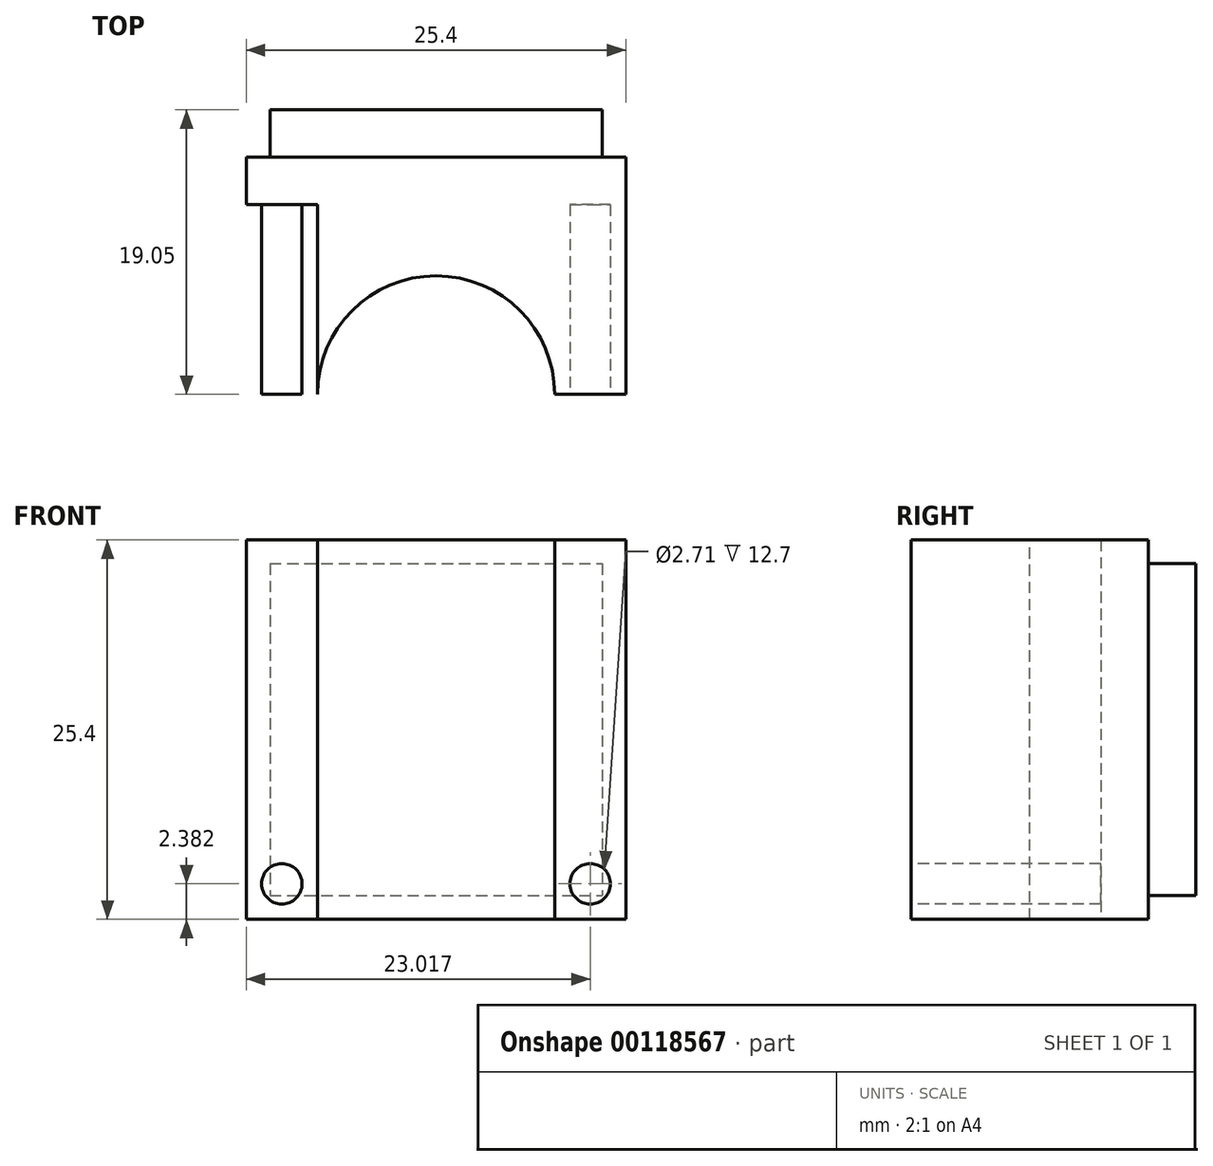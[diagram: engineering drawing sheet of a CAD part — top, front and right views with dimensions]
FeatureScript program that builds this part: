
annotation { "Feature Type Name" : "Feature", "Feature Type Description" : "" }
export const myFeature = defineFeature(function(context is Context, id is Id, definition is map)
    precondition{}
    {
        {
            var Q0;
            Q0=qCreatedBy(makeId("Front.planeOp"),FACE);
            var sketch = newSketch(context, id + "F0", { "sketchPlane" : qUnion([Q0])});
            skLineSegment(sketch, "E0.bottom", {"start": v(12.7, 12.7) * mm, "end": v(-12.7, 12.7) * mm});
            skLineSegment(sketch, "E0.top", {"start": v(12.7, -12.7) * mm, "end": v(-12.7, -12.7) * mm});
            skLineSegment(sketch, "E0.left", {"start": v(12.7, 12.7) * mm, "end": v(12.7, -12.7) * mm});
            skLineSegment(sketch, "E0.right", {"start": v(-12.7, 12.7) * mm, "end": v(-12.7, -12.7) * mm});
            skPoint(sketch, "E0.middle", {"position": v(0, 0) * mm});
            skSolve(sketch);
        }
        {
            var Q0;
            Q0 = qSketchRegion(id + "F0", true);
            extrude(context, id + "F1", {"entities" : qUnion([Q0]), "oppositeDirection" : true, "depth" : 19.05 * mm});
        }
        {
            var Q0;
            Q0=makeQuery(id+"F1.opExtrude","SWEPT_FACE",FACE,{"disambiguationData":[OSD([sQuery(id+"F0.wireOp",EDGE,"E0.bottom")])]});
            var sketch = newSketch(context, id + "F2", { "sketchPlane" : qUnion([Q0])});
            skCircle(sketch, "E1", {"center": v(0, 0) * mm, "radius": 7.94 * mm});
            skSolve(sketch);
        }
        {
            var Q0;
            Q0 = qSketchRegion(id + "F2", true);
            extrude(context, id + "F3", {"entities" : qUnion([Q0]), "operationType" : NewBodyOperationType.REMOVE, "endBound" : BoundingType.THROUGH_ALL, "oppositeDirection" : true, "depth" : 25.4 * mm});
        }
        {
            var Q0;
            Q0=makeQuery(id+"F1.opExtrude","CAP_FACE",FACE,{"disambiguationData":[OSD([sQuery(id+"F0.wireOp",EDGE,"E0.bottom"),sQuery(id+"F0.wireOp",EDGE,"E0.top"),sQuery(id+"F0.wireOp",EDGE,"E0.left"),sQuery(id+"F0.wireOp",EDGE,"E0.right")])],"isStart":false});
            var sketch = newSketch(context, id + "F4", { "sketchPlane" : qUnion([Q0])});
            skLineSegment(sketch, "E2.bottom", {"start": v(11.11, 11.11) * mm, "end": v(-11.11, 11.11) * mm});
            skLineSegment(sketch, "E2.top", {"start": v(11.11, -11.11) * mm, "end": v(-11.11, -11.11) * mm});
            skLineSegment(sketch, "E2.left", {"start": v(11.11, 11.11) * mm, "end": v(11.11, -11.11) * mm});
            skLineSegment(sketch, "E2.right", {"start": v(-11.11, 11.11) * mm, "end": v(-11.11, -11.11) * mm});
            skPoint(sketch, "E2.middle", {"position": v(0, 0) * mm});
            skSolve(sketch);
        }
        {
            var Q0;
            Q0=makeQuery(id+"F4.imprint","IMPRINT",FACE,{"disambiguationData":[TD([[makeQuery(id+"F4.imprint","IMPRINT",EDGE,{"derivedFrom":sQuery(id+"F4.wireOp",EDGE,"E2.bottom")}),-1.0]])]});
            extrude(context, id + "F5", {"entities" : qUnion([Q0]), "operationType" : NewBodyOperationType.REMOVE, "oppositeDirection" : true, "depth" : 3.17 * mm});
        }
        {
            var Q0;
            {var subQ0=sQuery(id+"F0.wireOp",EDGE,"E0.bottom");var subQ1=sQuery(id+"F0.wireOp",EDGE,"E0.top");var subQ2=sQuery(id+"F0.wireOp",EDGE,"E0.right");Q0=makeQuery(id+"F3.boolean.opBoolean","SPLIT",FACE,{"disambiguationData":[TD([makeQuery(id+"F1.opExtrude","SWEPT_FACE",FACE,{"disambiguationData":[OSD([subQ2])]})])],"derivedFrom":makeQuery(id+"F1.opExtrude","CAP_FACE",FACE,{"disambiguationData":[OSD([subQ0,subQ1,sQuery(id+"F0.wireOp",EDGE,"E0.left"),subQ2])],"isStart":true})});}
            var sketch = newSketch(context, id + "F6", { "sketchPlane" : qUnion([Q0])});
            skCircle(sketch, "E3", {"center": v(-10.32, 10.32) * mm, "radius": 1.35 * mm});
            skCircle(sketch, "E4.MirrorC", {"center": v(10.32, 10.32) * mm, "radius": 1.35 * mm});
            skCircle(sketch, "E5.MirrorC", {"center": v(10.32, -10.32) * mm, "radius": 1.35 * mm});
            skCircle(sketch, "E6.MirrorC", {"center": v(-10.32, -10.32) * mm, "radius": 1.35 * mm});
            skSolve(sketch);
        }
        {
            var Q0;
            Q0=makeQuery(id+"F6.imprint","IMPRINT",FACE,{"disambiguationData":[TD([[makeQuery(id+"F6.imprint","IMPRINT",EDGE,{"derivedFrom":sQuery(id+"F6.wireOp",EDGE,"E3")}),1.0]])]});
            var Q1;
            Q1=makeQuery(id+"F6.imprint","IMPRINT",FACE,{"disambiguationData":[TD([[makeQuery(id+"F6.imprint","IMPRINT",EDGE,{"derivedFrom":sQuery(id+"F6.wireOp",EDGE,"E6.MirrorC")}),-1.0]])]});
            var Q2;
            Q2=makeQuery(id+"F6.imprint","IMPRINT",FACE,{"disambiguationData":[TD([[makeQuery(id+"F6.imprint","IMPRINT",EDGE,{"derivedFrom":sQuery(id+"F6.wireOp",EDGE,"E4.MirrorC")}),-1.0]])]});
            var Q3;
            Q3=makeQuery(id+"F6.imprint","IMPRINT",FACE,{"disambiguationData":[TD([[makeQuery(id+"F6.imprint","IMPRINT",EDGE,{"derivedFrom":sQuery(id+"F6.wireOp",EDGE,"E5.MirrorC")}),1.0]])]});
            extrude(context, id + "F7", {"entities" : qUnion([Q0, Q1, Q2, Q3]), "operationType" : NewBodyOperationType.REMOVE, "oppositeDirection" : true, "depth" : 12.7 * mm});
        }
    });
